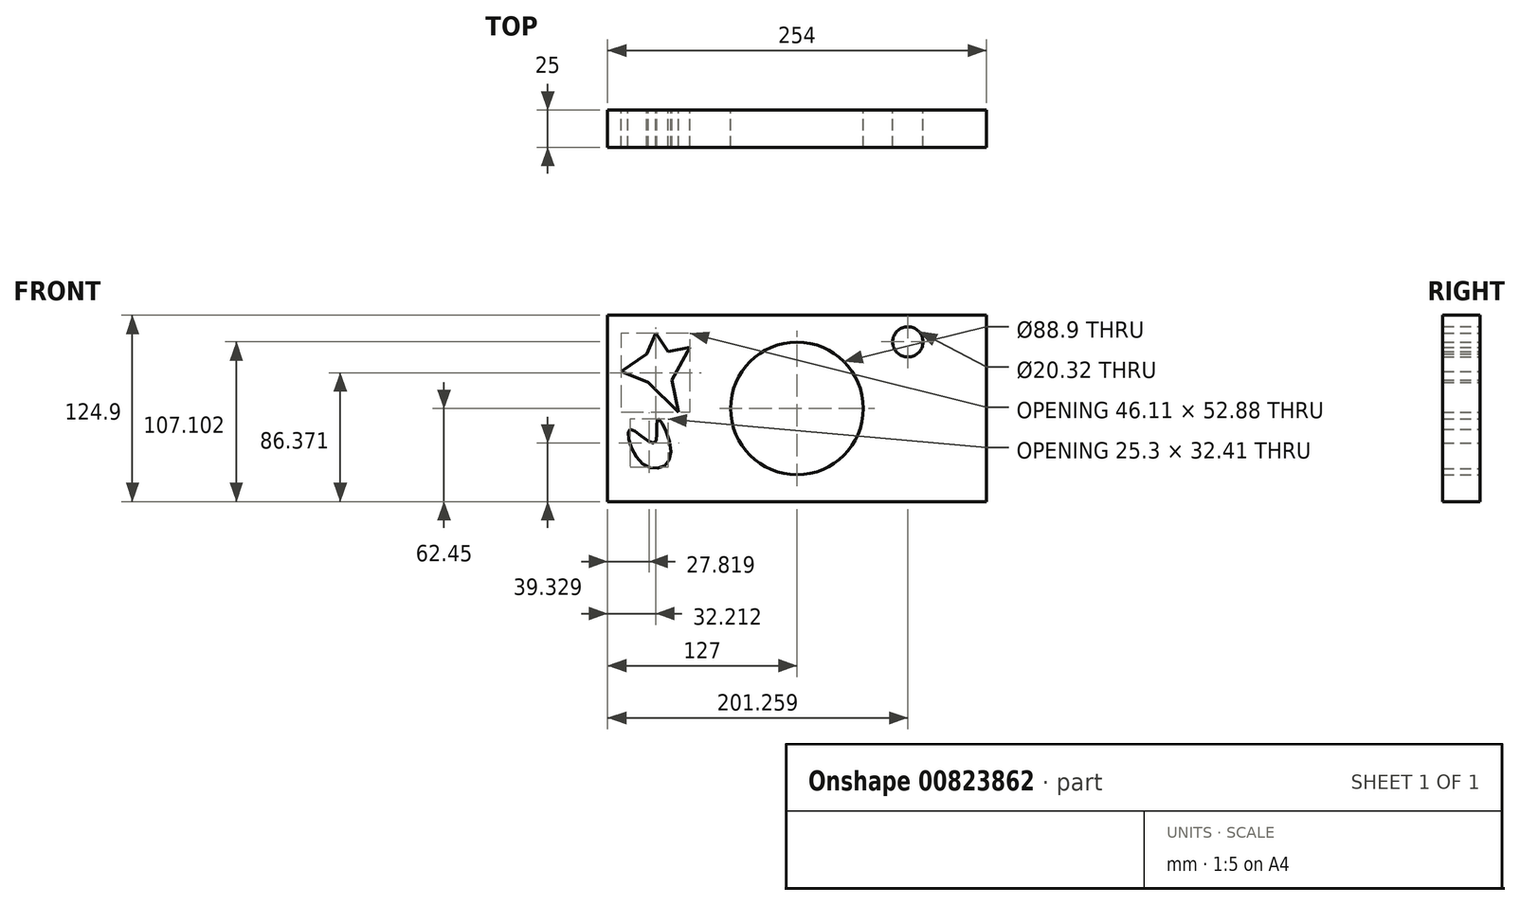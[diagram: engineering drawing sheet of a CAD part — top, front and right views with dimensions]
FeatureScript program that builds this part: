
annotation { "Feature Type Name" : "Feature", "Feature Type Description" : "" }
export const myFeature = defineFeature(function(context is Context, id is Id, definition is map)
    precondition{}
    {
        {
            var Q0;
            Q0=qCreatedBy(makeId("Front.planeOp"),FACE);
            var sketch = newSketch(context, id + "F0", { "sketchPlane" : qUnion([Q0])});
            skLineSegment(sketch, "E0.bottom", {"start": v(-127, 62.45) * mm, "end": v(127, 62.45) * mm});
            skLineSegment(sketch, "E0.top", {"start": v(-127, -62.45) * mm, "end": v(127, -62.45) * mm});
            skLineSegment(sketch, "E0.left", {"start": v(-127, 62.45) * mm, "end": v(-127, -62.45) * mm});
            skLineSegment(sketch, "E0.right", {"start": v(127, 62.45) * mm, "end": v(127, -62.45) * mm});
            skPoint(sketch, "E0.middle", {"position": v(0, 0) * mm});
            skCircle(sketch, "E1", {"center": v(0, 0) * mm, "radius": 44.45 * mm});
            skCircle(sketch, "E2", {"center": v(74.26, 44.65) * mm, "radius": 10.16 * mm});
            skLineSegment(sketch, "E3", {"start": v(-100.8, 36.58) * mm, "end": v(-94.79, 50.36) * mm});
            skLineSegment(sketch, "E4", {"start": v(-94.79, 50.36) * mm, "end": v(-86.52, 38.08) * mm});
            skLineSegment(sketch, "E5", {"start": v(-86.52, 38.08) * mm, "end": v(-71.73, 40.84) * mm});
            skLineSegment(sketch, "E6", {"start": v(-71.73, 40.84) * mm, "end": v(-83.76, 19.03) * mm});
            skLineSegment(sketch, "E7", {"start": v(-83.76, 19.03) * mm, "end": v(-79.5, -2.52) * mm});
            skLineSegment(sketch, "E8", {"start": v(-79.5, -2.52) * mm, "end": v(-99.8, 17.53) * mm});
            skLineSegment(sketch, "E9", {"start": v(-99.8, 17.53) * mm, "end": v(-117.84, 24.8) * mm});
            skLineSegment(sketch, "E10", {"start": v(-117.84, 24.8) * mm, "end": v(-100.8, 36.58) * mm});
            skFitSpline(sketch, "E11", {"points": [v(-111.83, -14.05) * mm, v(-95.54, -23.07) * mm, v(-93.54, -7.03) * mm, v(-85.01, -32.6) * mm, v(-103.56, -37.1) * mm, v(-111.83, -14.05) * mm]});
            skSolve(sketch);
        }
        {
            var Q0;
            Q0=makeQuery(id+"F0.imprint","IMPRINT",FACE,{"disambiguationData":[TD([[makeQuery(id+"F0.imprint","IMPRINT",EDGE,{"derivedFrom":sQuery(id+"F0.wireOp",EDGE,"E0.bottom")}),-1.0]])]});
            extrude(context, id + "F1", {"entities" : qUnion([Q0]), "depth" : 25 * mm, "offsetDistance" : 25 * mm});
        }
    });
